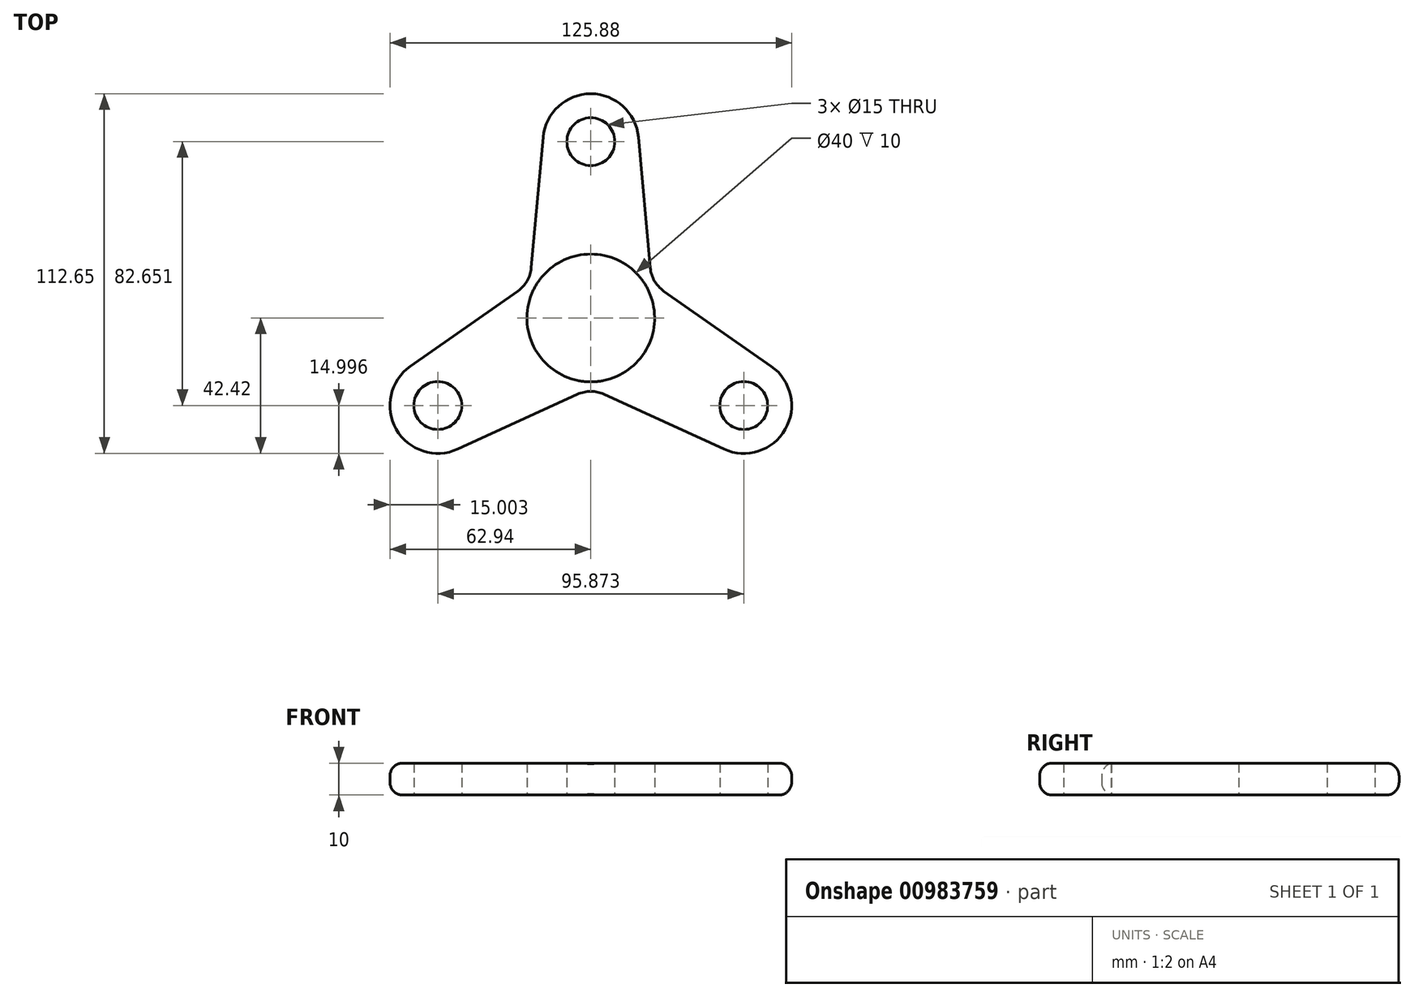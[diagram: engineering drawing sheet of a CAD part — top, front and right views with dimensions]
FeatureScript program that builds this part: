
annotation { "Feature Type Name" : "Feature", "Feature Type Description" : "" }
export const myFeature = defineFeature(function(context is Context, id is Id, definition is map)
    precondition{}
    {
        {
            var Q0;
            Q0=qCreatedBy(makeId("Top.planeOp"),FACE);
            var sketch = newSketch(context, id + "F0", { "sketchPlane" : qUnion([Q0])});
            skCircle(sketch, "E0", {"center": v(0, 0) * mm, "radius": 20 * mm});
            skPoint(sketch, "E1", {"position": v(-47.94, -27.42) * mm});
            skPoint(sketch, "E2", {"position": v(47.94, -27.42) * mm});
            skPoint(sketch, "E3", {"position": v(0, 55.23) * mm});
            skCircle(sketch, "E4", {"center": v(-47.94, -27.42) * mm, "radius": 15 * mm});
            skCircle(sketch, "E5", {"center": v(47.94, -27.42) * mm, "radius": 15 * mm});
            skCircle(sketch, "E6", {"center": v(0, 55.23) * mm, "radius": 15 * mm});
            skLineSegment(sketch, "E7", {"start": v(-22.88, 8.4) * mm, "end": v(-56.53, -15.13) * mm});
            skLineSegment(sketch, "E8", {"start": v(-4.16, -23.9) * mm, "end": v(-41.7, -41.07) * mm});
            skLineSegment(sketch, "E9", {"start": v(-18.66, 15.7) * mm, "end": v(-14.94, 56.58) * mm});
            skLineSegment(sketch, "E10", {"start": v(18.66, 15.7) * mm, "end": v(14.94, 56.58) * mm});
            skLineSegment(sketch, "E11", {"start": v(22.88, 8.4) * mm, "end": v(56.53, -15.13) * mm});
            skLineSegment(sketch, "E12", {"start": v(4.16, -23.9) * mm, "end": v(41.7, -41.07) * mm});
            skPoint(sketch, "E13", {"position": v(-12.38, -27.66) * mm});
            skPoint(sketch, "E14", {"position": v(12.38, -27.66) * mm});
            skArc(sketch, "E15.filletArc", {"start": v(-22.88, 8.4) * mm, "mid": v(-19.96, 11.58) * mm, "end": v(-18.66, 15.7) * mm});
            skPoint(sketch, "E16.newPointA", {"position": v(11.46, 16.39) * mm});
            skArc(sketch, "E16.filletArc", {"start": v(18.66, 15.7) * mm, "mid": v(19.96, 11.58) * mm, "end": v(22.88, 8.4) * mm});
            skPoint(sketch, "E17.newPointA", {"position": v(-8.32, -18.19) * mm});
            skArc(sketch, "E17.filletArc", {"start": v(4.16, -23.9) * mm, "mid": v(0, -22.99) * mm, "end": v(-4.16, -23.9) * mm});
            skCircle(sketch, "E18", {"center": v(0, 55.23) * mm, "radius": 7.5 * mm});
            skCircle(sketch, "E19", {"center": v(-47.94, -27.42) * mm, "radius": 7.5 * mm});
            skCircle(sketch, "E20", {"center": v(47.94, -27.42) * mm, "radius": 7.5 * mm});
            skSolve(sketch);
        }
        {
            var Q0;
            Q0 = qSketchRegion(id + "F0", true);
            extrude(context, id + "F1", {"entities" : qUnion([Q0]), "depth" : 10 * mm, "offsetDistance" : 25 * mm});
        }
        {
            var Q0;
            Q0=makeQuery(id+"F1.opExtrude","CAP_EDGE",EDGE,{"disambiguationData":[OSD([sQuery(id+"F0.wireOp",EDGE,"E8")])],"isStart":false});
            var Q1;
            Q1=makeQuery(id+"F1.opExtrude","CAP_EDGE",EDGE,{"disambiguationData":[OSD([sQuery(id+"F0.wireOp",EDGE,"E8")])],"isStart":true});
            fillet(context, id + "F2", {"entities" : qUnion([Q0, Q1]), "radius" : 4 * mm, "tangentPropagation" : true, "allowEdgeOverflow" : false});
        }
    });
